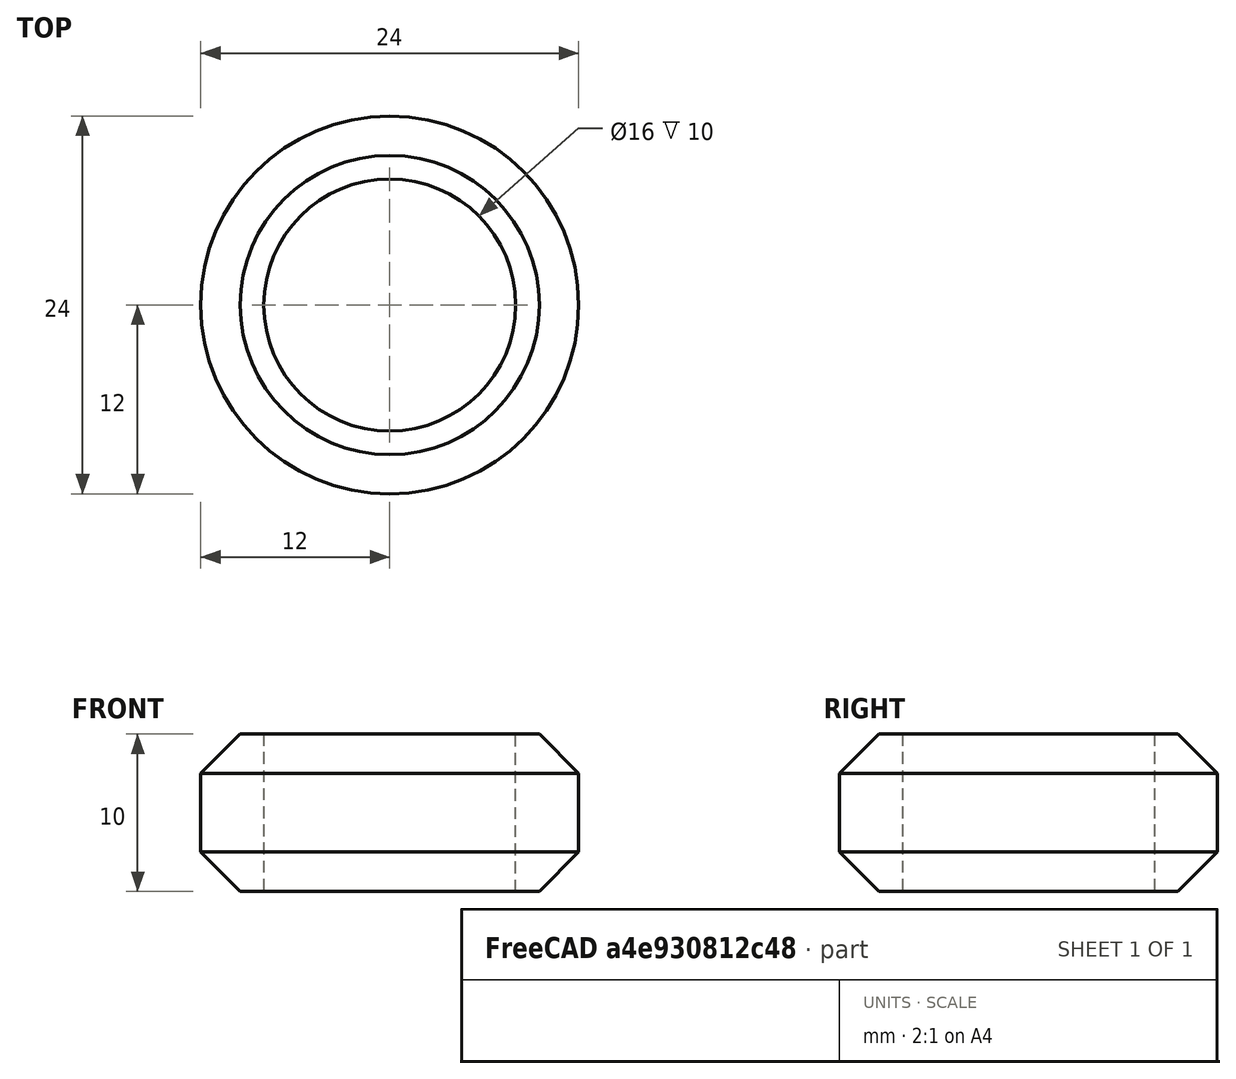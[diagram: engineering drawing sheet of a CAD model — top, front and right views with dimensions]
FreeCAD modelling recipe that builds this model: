
FCSTD DOCUMENT  (FreeCAD 0.21R33771 (Git))
Label: pulleyWheel
License: All rights reserved
LicenseURL: http://en.wikipedia.org/wiki/All_rights_reserved
objects: Sketcher::SketchObject×1, PartDesign::Pad×1, PartDesign::Chamfer×1, PartDesign::Body×1
note: 6 computed .brp shape members not serialized (recipe doc carries the construction recipe); baked Part::Feature solids carry a one-line shape summary decoded from their .brp

FEATURE [Sketcher::SketchObject] Sketch
  FullyConstrained = true
  MapMode = 5
  Support = -> [XY_Plane]
  sketch-geometry (2):
    g0: Circle CenterX=0 CenterY=0 CenterZ=0 NormalX=0 NormalY=0 NormalZ=1 AngleXU=0 Radius=8
    g1: Circle CenterX=0 CenterY=0 CenterZ=0 NormalX=0 NormalY=0 NormalZ=1 AngleXU=0 Radius=12
  constraints (4):
    c: Coincident(g0,g-1)
    c: Coincident(g1,g0)
    c: Diameter(g0) = 16
    c: Diameter(g1) = 24
FEATURE [PartDesign::Pad] Pad
  Direction = (0,0,1)
  Length = 10
  Length2 = 10
  Profile = -> Sketch
  ReferenceAxis = -> Sketch [N_Axis]
  Refine = true
  Type = 0
FEATURE [PartDesign::Chamfer] Chamfer
  Angle = 45
  Base = -> Pad [Edge3,Edge2]
  BaseFeature = -> Pad
  ChamferType = 0
  FlipDirection = false
  Refine = true
  Size = 2.5
  Size2 = 1
  SupportTransform = false
  UseAllEdges = false
FEATURE [PartDesign::Body] Body
  Group = -> [Sketch,Pad,Chamfer]
  Origin = -> Origin
  Tip = -> Chamfer
